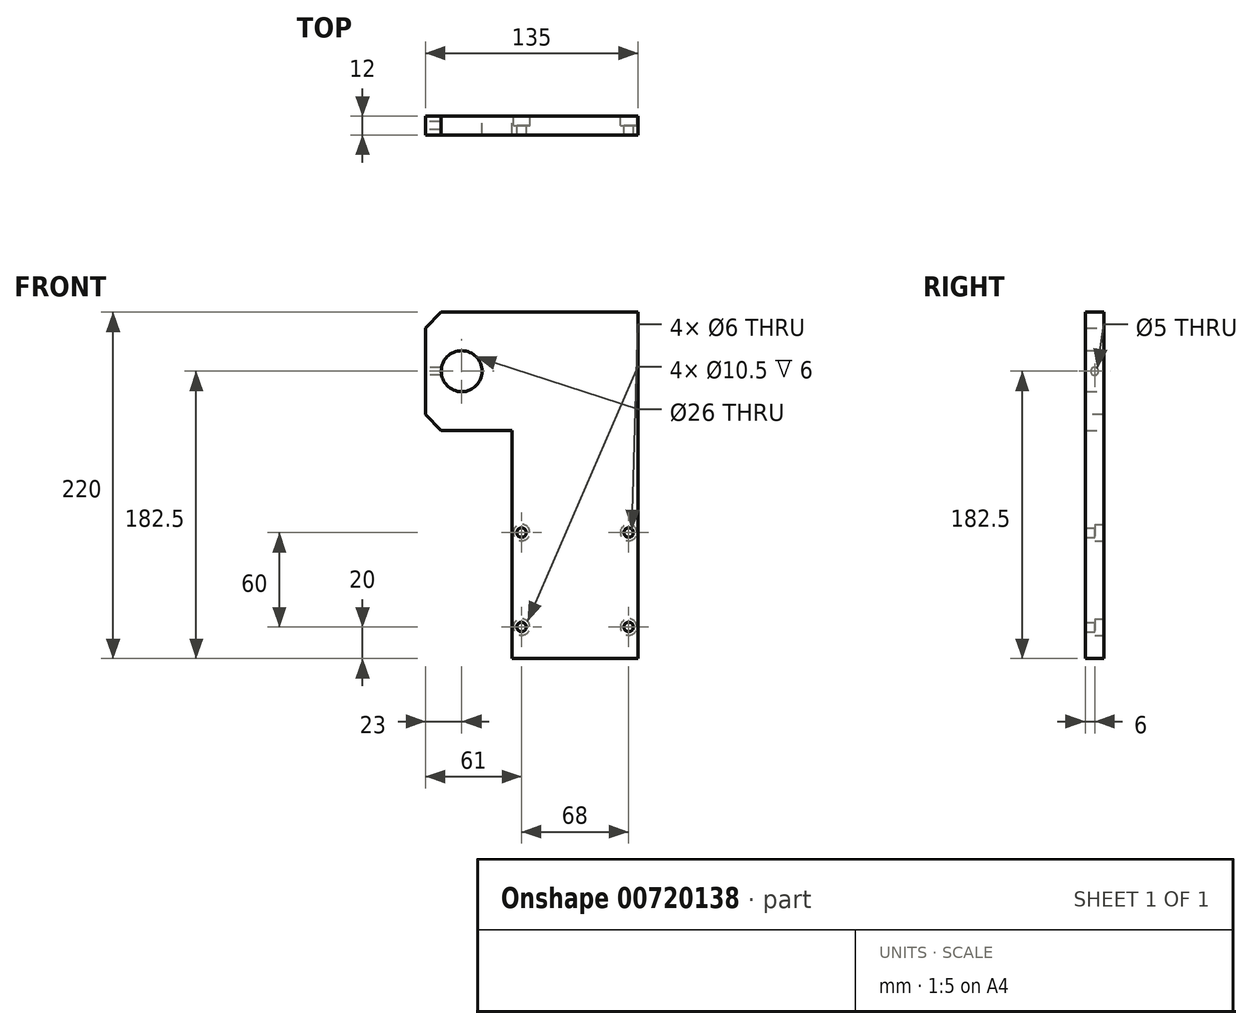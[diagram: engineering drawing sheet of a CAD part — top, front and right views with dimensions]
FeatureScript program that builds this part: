
annotation { "Feature Type Name" : "Feature", "Feature Type Description" : "" }
export const myFeature = defineFeature(function(context is Context, id is Id, definition is map)
    precondition{}
    {
        {
            var Q0;
            Q0=qCreatedBy(makeId("Front.planeOp"),FACE);
            var sketch = newSketch(context, id + "F0", { "sketchPlane" : qUnion([Q0])});
            skLineSegment(sketch, "E0", {"start": v(0, 0) * mm, "end": v(80, 0) * mm});
            skLineSegment(sketch, "E1", {"start": v(80, 0) * mm, "end": v(80, 220) * mm});
            skLineSegment(sketch, "E2", {"start": v(80, 220) * mm, "end": v(-55, 220) * mm});
            skLineSegment(sketch, "E3", {"start": v(-55, 220) * mm, "end": v(-55, 145) * mm});
            skLineSegment(sketch, "E4", {"start": v(-55, 145) * mm, "end": v(0, 145) * mm});
            skLineSegment(sketch, "E5", {"start": v(0, 145) * mm, "end": v(0, 0) * mm});
            skCircle(sketch, "E6", {"center": v(-32, 182.5) * mm, "radius": 13 * mm});
            skPoint(sketch, "E6.centerSnap0", {"position": v(-55, 182.5) * mm});
            skCircle(sketch, "E7", {"center": v(6, 20) * mm, "radius": 3 * mm});
            skCircle(sketch, "E8", {"center": v(6, 80) * mm, "radius": 3 * mm});
            skCircle(sketch, "E9", {"center": v(74, 80) * mm, "radius": 3 * mm});
            skCircle(sketch, "E10", {"center": v(74, 20) * mm, "radius": 3 * mm});
            skSolve(sketch);
        }
        {
            var Q0;
            Q0=makeQuery(id+"F0.imprint","IMPRINT",FACE,{"disambiguationData":[TD([[makeQuery(id+"F0.imprint","IMPRINT",EDGE,{"derivedFrom":sQuery(id+"F0.wireOp",EDGE,"E0")}),1.0]])]});
            extrude(context, id + "F1", {"entities" : qUnion([Q0]), "depth" : 12 * mm, "offsetDistance" : 25 * mm});
        }
        {
            var Q0;
            Q0=makeQuery(id+"F1.opExtrude","SWEPT_EDGE",EDGE,{"disambiguationData":[OSD([sQuery(id+"F0.wireOp",EDGE,"E2"),sQuery(id+"F0.wireOp",EDGE,"E3")])]});
            var Q1;
            Q1=makeQuery(id+"F1.opExtrude","SWEPT_EDGE",EDGE,{"disambiguationData":[OSD([sQuery(id+"F0.wireOp",EDGE,"E3"),sQuery(id+"F0.wireOp",EDGE,"E4")])]});
            chamfer(context, id + "F2", {"entities" : qUnion([Q0, Q1]), "width" : 10 * mm, "tangentPropagation" : true});
        }
        {
            var Q0;
            Q0=makeQuery(id+"F1.opExtrude","SWEPT_FACE",FACE,{"disambiguationData":[OSD([sQuery(id+"F0.wireOp",EDGE,"E3")])]});
            var sketch = newSketch(context, id + "F3", { "sketchPlane" : qUnion([Q0])});
            skCircle(sketch, "E11", {"center": v(6, 182.5) * mm, "radius": 2.5 * mm});
            skPoint(sketch, "E11.centerSnap0", {"position": v(12, 182.5) * mm});
            skPoint(sketch, "E11.centerSnap1", {"position": v(6, 210) * mm});
            skSolve(sketch);
        }
        {
            var Q0;
            Q0=makeQuery(id+"F3.imprint","IMPRINT",FACE,{"disambiguationData":[TD([[makeQuery(id+"F3.imprint","IMPRINT",EDGE,{"derivedFrom":sQuery(id+"F3.wireOp",EDGE,"E11")}),1.0]])]});
            extrude(context, id + "F4", {"entities" : qUnion([Q0]), "operationType" : NewBodyOperationType.REMOVE, "oppositeDirection" : true, "depth" : 25 * mm, "offsetDistance" : 25 * mm});
        }
        {
            var Q0;
            Q0=makeQuery(id+"F1.opExtrude","CAP_FACE",FACE,{"disambiguationData":[OSD([sQuery(id+"F0.wireOp",EDGE,"E0"),sQuery(id+"F0.wireOp",EDGE,"E1"),sQuery(id+"F0.wireOp",EDGE,"E2"),sQuery(id+"F0.wireOp",EDGE,"E3"),sQuery(id+"F0.wireOp",EDGE,"E4"),sQuery(id+"F0.wireOp",EDGE,"E5"),sQuery(id+"F0.wireOp",EDGE,"E6"),sQuery(id+"F0.wireOp",EDGE,"E7"),sQuery(id+"F0.wireOp",EDGE,"E8"),sQuery(id+"F0.wireOp",EDGE,"E9"),sQuery(id+"F0.wireOp",EDGE,"E10")])],"isStart":true});
            var sketch = newSketch(context, id + "F5", { "sketchPlane" : qUnion([Q0])});
            skCircle(sketch, "E12", {"center": v(-74, 80) * mm, "radius": 5.25 * mm});
            skCircle(sketch, "E13", {"center": v(-6, 80) * mm, "radius": 5.25 * mm});
            skCircle(sketch, "E14", {"center": v(-6, 20) * mm, "radius": 5.25 * mm});
            skCircle(sketch, "E15", {"center": v(-74, 20) * mm, "radius": 5.25 * mm});
            skSolve(sketch);
        }
        {
            var Q0;
            Q0=makeQuery(id+"F5.imprint","IMPRINT",FACE,{"disambiguationData":[TD([[makeQuery(id+"F5.imprint","IMPRINT",EDGE,{"derivedFrom":sQuery(id+"F5.wireOp",EDGE,"E12")}),1.0]])]});
            var Q1;
            Q1=makeQuery(id+"F5.imprint","IMPRINT",FACE,{"disambiguationData":[TD([[makeQuery(id+"F5.imprint","IMPRINT",EDGE,{"derivedFrom":sQuery(id+"F5.wireOp",EDGE,"E13")}),1.0]])]});
            var Q2;
            Q2=makeQuery(id+"F5.imprint","IMPRINT",FACE,{"disambiguationData":[TD([[makeQuery(id+"F5.imprint","IMPRINT",EDGE,{"derivedFrom":sQuery(id+"F5.wireOp",EDGE,"E14")}),1.0]])]});
            var Q3;
            Q3=makeQuery(id+"F5.imprint","IMPRINT",FACE,{"disambiguationData":[TD([[makeQuery(id+"F5.imprint","IMPRINT",EDGE,{"derivedFrom":sQuery(id+"F5.wireOp",EDGE,"E15")}),1.0]])]});
            extrude(context, id + "F6", {"entities" : qUnion([Q0, Q1, Q2, Q3]), "operationType" : NewBodyOperationType.REMOVE, "oppositeDirection" : true, "depth" : 6 * mm, "offsetDistance" : 25 * mm});
        }
    });
